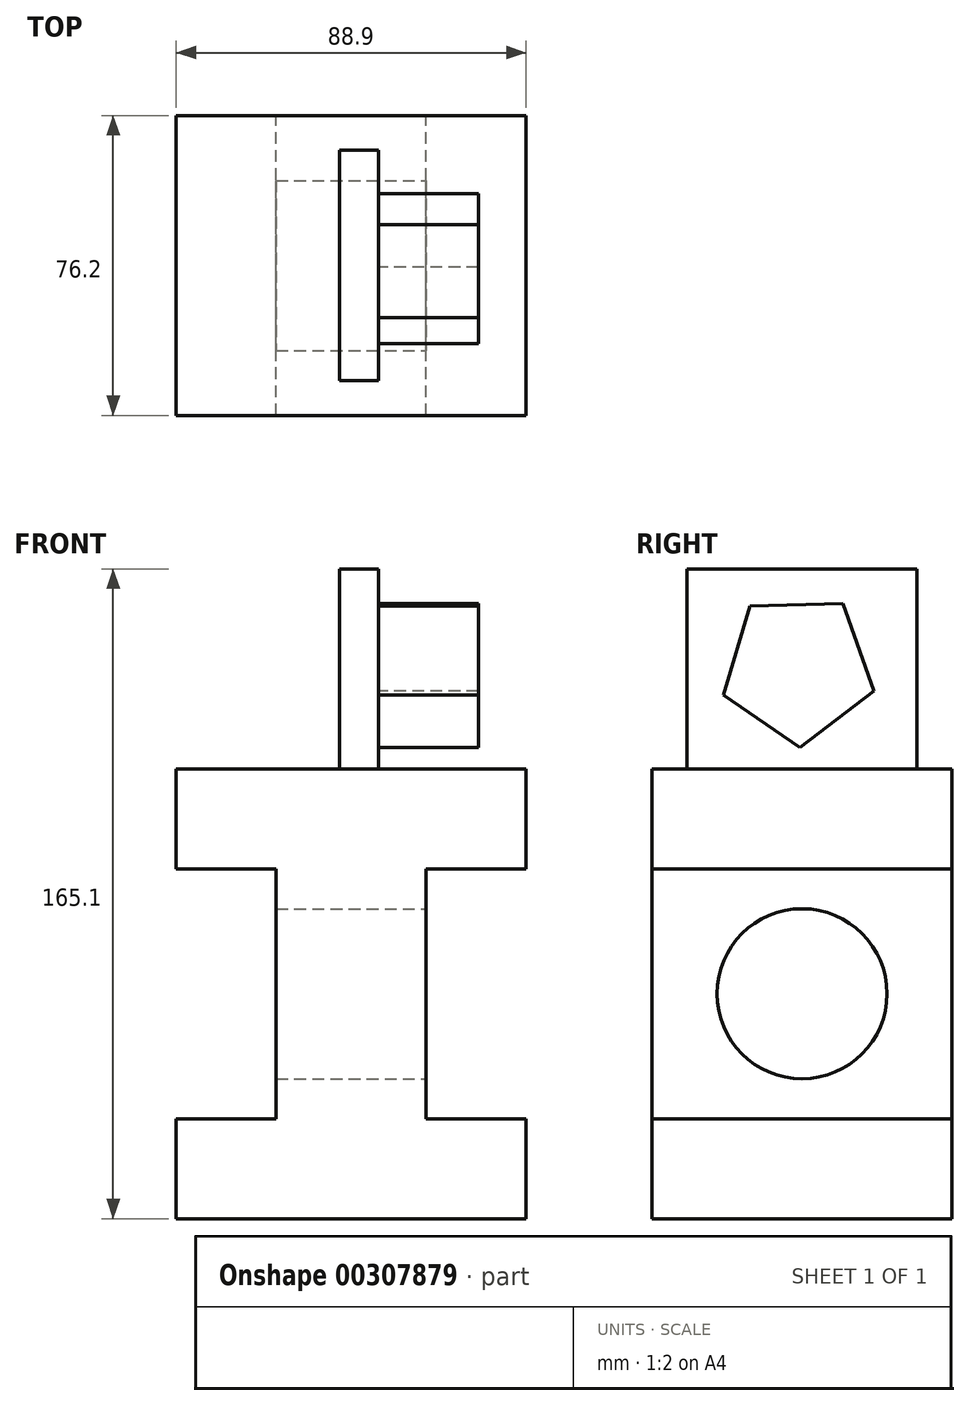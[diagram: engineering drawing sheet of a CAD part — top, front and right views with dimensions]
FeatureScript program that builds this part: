
annotation { "Feature Type Name" : "Feature", "Feature Type Description" : "" }
export const myFeature = defineFeature(function(context is Context, id is Id, definition is map)
    precondition{}
    {
        {
            var Q0;
            Q0=qCreatedBy(makeId("Front.planeOp"),FACE);
            var sketch = newSketch(context, id + "F0", { "sketchPlane" : qUnion([Q0])});
            skLineSegment(sketch, "E0", {"start": v(-46.43, -38.63) * mm, "end": v(42.47, -38.63) * mm});
            skLineSegment(sketch, "E1", {"start": v(42.47, -38.63) * mm, "end": v(42.47, -13.23) * mm});
            skLineSegment(sketch, "E2", {"start": v(42.47, -13.23) * mm, "end": v(17.07, -13.23) * mm});
            skLineSegment(sketch, "E3", {"start": v(17.07, -13.23) * mm, "end": v(17.07, 50.27) * mm});
            skLineSegment(sketch, "E4", {"start": v(17.07, 50.27) * mm, "end": v(42.47, 50.27) * mm});
            skLineSegment(sketch, "E5", {"start": v(42.47, 50.27) * mm, "end": v(42.47, 75.67) * mm});
            skLineSegment(sketch, "E6", {"start": v(42.47, 75.67) * mm, "end": v(-46.43, 75.67) * mm});
            skLineSegment(sketch, "E7", {"start": v(-46.43, 75.67) * mm, "end": v(-46.43, 50.27) * mm});
            skLineSegment(sketch, "E8", {"start": v(-46.43, 50.27) * mm, "end": v(-21.03, 50.27) * mm});
            skLineSegment(sketch, "E9", {"start": v(-21.03, 50.27) * mm, "end": v(-21.03, -13.23) * mm});
            skLineSegment(sketch, "E10", {"start": v(-21.03, -13.23) * mm, "end": v(-46.43, -13.23) * mm});
            skLineSegment(sketch, "E11", {"start": v(-46.43, -13.23) * mm, "end": v(-46.43, -38.63) * mm});
            skSolve(sketch);
        }
        {
            var Q0;
            Q0=makeQuery(id+"F0.imprint","IMPRINT",FACE,{"disambiguationData":[TD([[makeQuery(id+"F0.imprint","IMPRINT",EDGE,{"derivedFrom":sQuery(id+"F0.wireOp",EDGE,"E0")}),1.0]])]});
            extrude(context, id + "F1", {"entities" : qUnion([Q0]), "depth" : 76.2 * mm});
        }
        {
            var Q0;
            Q0=makeQuery(id+"F1.opExtrude","SWEPT_FACE",FACE,{"disambiguationData":[OSD([sQuery(id+"F0.wireOp",EDGE,"E3")])]});
            var sketch = newSketch(context, id + "F2", { "sketchPlane" : qUnion([Q0])});
            skCircle(sketch, "E12", {"center": v(-38.1, 18.52) * mm, "radius": 21.6 * mm});
            skPoint(sketch, "E12.centerSnap0", {"position": v(-38.1, 50.27) * mm});
            skPoint(sketch, "E12.centerSnap1", {"position": v(-76.2, 18.52) * mm});
            skSolve(sketch);
        }
        {
            var Q0;
            Q0=makeQuery(id+"F2.imprint","IMPRINT",FACE,{"disambiguationData":[TD([[makeQuery(id+"F2.imprint","IMPRINT",EDGE,{"derivedFrom":sQuery(id+"F2.wireOp",EDGE,"E12")}),1.0]])]});
            extrude(context, id + "F3", {"entities" : qUnion([Q0]), "operationType" : NewBodyOperationType.REMOVE, "endBound" : BoundingType.THROUGH_ALL, "oppositeDirection" : true, "depth" : 25.4 * mm});
        }
        {
            var Q0;
            Q0=makeQuery(id+"F1.opExtrude","SWEPT_FACE",FACE,{"disambiguationData":[OSD([sQuery(id+"F0.wireOp",EDGE,"E6")])]});
            var sketch = newSketch(context, id + "F4", { "sketchPlane" : qUnion([Q0])});
            skLineSegment(sketch, "E13.bottom", {"start": v(4.95, -67.32) * mm, "end": v(-4.95, -67.32) * mm});
            skLineSegment(sketch, "E13.top", {"start": v(4.95, -8.88) * mm, "end": v(-4.95, -8.88) * mm});
            skLineSegment(sketch, "E13.left", {"start": v(4.95, -67.32) * mm, "end": v(4.95, -8.88) * mm});
            skLineSegment(sketch, "E13.right", {"start": v(-4.95, -67.32) * mm, "end": v(-4.95, -8.88) * mm});
            skPoint(sketch, "E13.middle", {"position": v(0, -38.1) * mm});
            skPoint(sketch, "E13.middle.positionSnap0", {"position": v(-46.43, -38.1) * mm});
            skPoint(sketch, "E13.centerSnap0", {"position": v(-46.43, -38.1) * mm});
            skSolve(sketch);
        }
        {
            var Q0;
            Q0=makeQuery(id+"F4.imprint","IMPRINT",FACE,{"disambiguationData":[TD([[makeQuery(id+"F4.imprint","IMPRINT",EDGE,{"derivedFrom":sQuery(id+"F4.wireOp",EDGE,"E13.bottom")}),-1.0]])]});
            extrude(context, id + "F5", {"entities" : qUnion([Q0]), "operationType" : NewBodyOperationType.ADD, "depth" : 50.8 * mm});
        }
        {
            var Q0;
            Q0=makeQuery(id+"F5.opExtrude","SWEPT_FACE",FACE,{"disambiguationData":[OSD([sQuery(id+"F4.wireOp",EDGE,"E13.left")])]});
            var sketch = newSketch(context, id + "F6", { "sketchPlane" : qUnion([Q0])});
            skCircle(sketch, "E14.cCircle", {"center": v(-39.12, 101.07) * mm, "radius": 20.05 * mm, "construction": true});
            skPoint(sketch, "E14.cCircle.centerSnap0", {"position": v(-8.88, 101.07) * mm});
            skLineSegment(sketch, "E14.0", {"start": v(-27.76, 117.6) * mm, "end": v(-19.9, 95.37) * mm});
            skLineSegment(sketch, "E14.1", {"start": v(-19.9, 95.37) * mm, "end": v(-38.6, 81.03) * mm});
            skLineSegment(sketch, "E14.2", {"start": v(-38.6, 81.03) * mm, "end": v(-58.02, 94.38) * mm});
            skLineSegment(sketch, "E14.3", {"start": v(-58.02, 94.38) * mm, "end": v(-51.32, 116.98) * mm});
            skLineSegment(sketch, "E14.4", {"start": v(-51.32, 116.98) * mm, "end": v(-27.76, 117.6) * mm});
            skSolve(sketch);
        }
        {
            var Q0;
            Q0=makeQuery(id+"F6.imprint","IMPRINT",FACE,{"disambiguationData":[TD([[makeQuery(id+"F6.imprint","IMPRINT",EDGE,{"derivedFrom":sQuery(id+"F6.wireOp",EDGE,"E14.0")}),-1.0]])]});
            extrude(context, id + "F7", {"entities" : qUnion([Q0]), "operationType" : NewBodyOperationType.ADD, "depth" : 25.4 * mm});
        }
    });
